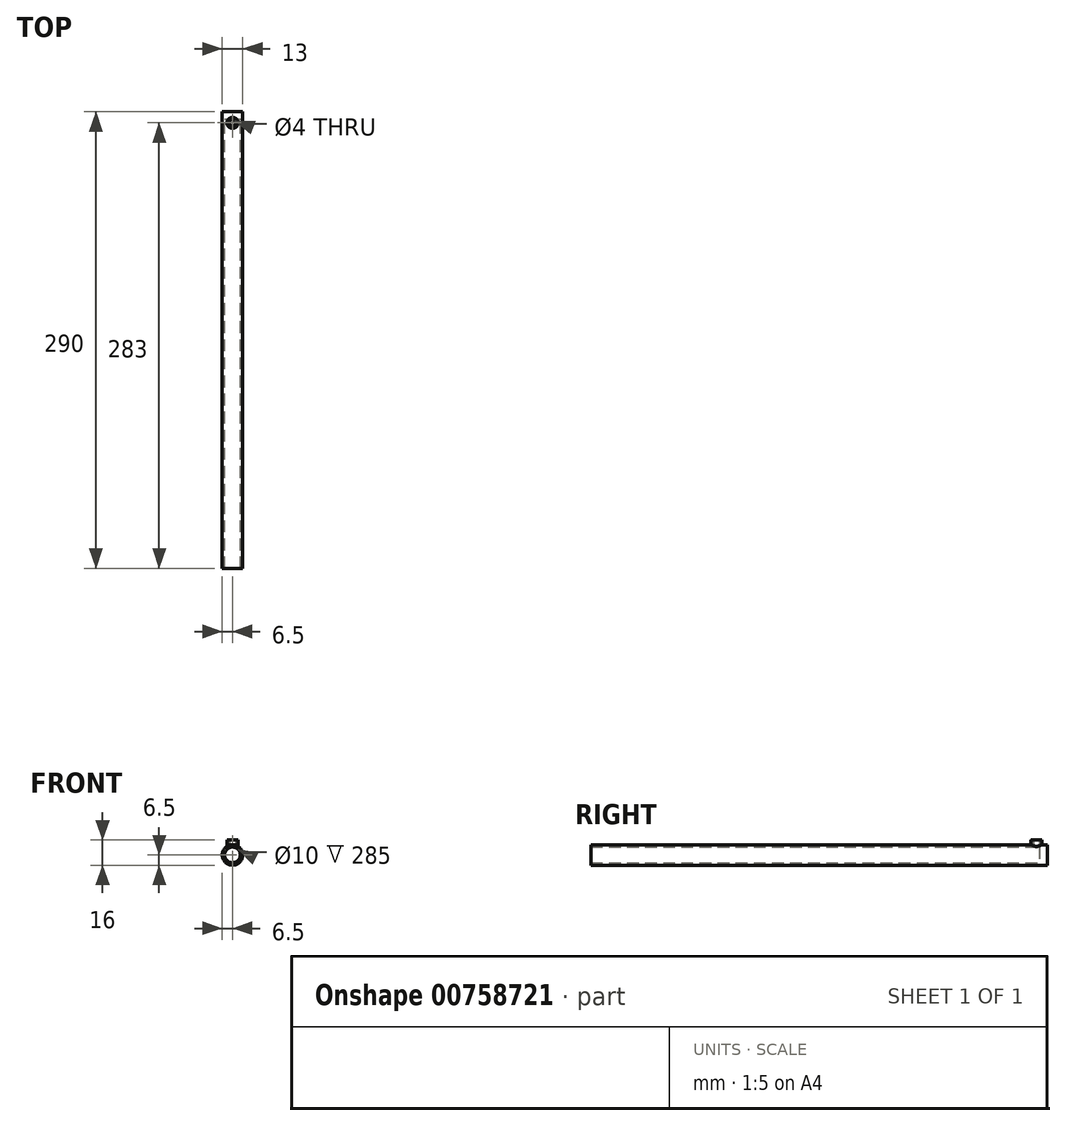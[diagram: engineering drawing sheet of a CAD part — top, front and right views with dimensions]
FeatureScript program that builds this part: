
annotation { "Feature Type Name" : "Feature", "Feature Type Description" : "" }
export const myFeature = defineFeature(function(context is Context, id is Id, definition is map)
    precondition{}
    {
        {
            var Q0;
            Q0=qCreatedBy(makeId("Front.planeOp"),FACE);
            var sketch = newSketch(context, id + "F0", { "sketchPlane" : qUnion([Q0])});
            skCircle(sketch, "E0", {"center": v(0, 0) * mm, "radius": 6.5 * mm});
            skCircle(sketch, "E1", {"center": v(0, 0) * mm, "radius": 5 * mm});
            skSolve(sketch);
        }
        {
            var Q0;
            Q0=makeQuery(id+"F0.imprint","IMPRINT",FACE,{"disambiguationData":[TD([[makeQuery(id+"F0.imprint","IMPRINT",EDGE,{"derivedFrom":sQuery(id+"F0.wireOp",EDGE,"E0")}),1.0]])]});
            extrude(context, id + "F1", {"entities" : qUnion([Q0]), "depth" : 290 * mm, "offsetDistance" : 25 * mm});
        }
        {
            var Q0;
            Q0=makeQuery(id+"F0.imprint","IMPRINT",FACE,{"disambiguationData":[TD([[makeQuery(id+"F0.imprint","IMPRINT",EDGE,{"derivedFrom":sQuery(id+"F0.wireOp",EDGE,"E1")}),1.0]])]});
            extrude(context, id + "F2", {"entities" : qUnion([Q0]), "operationType" : NewBodyOperationType.ADD, "depth" : 5 * mm, "offsetDistance" : 25 * mm});
        }
        {
            var Q0;
            Q0=qCreatedBy(makeId("Top.planeOp"),FACE);
            var sketch = newSketch(context, id + "F3", { "sketchPlane" : qUnion([Q0])});
            skLineSegment(sketch, "E2", {"start": v(0, 0) * mm, "end": v(0, -7) * mm});
            skCircle(sketch, "E3", {"center": v(0, -7) * mm, "radius": 2 * mm});
            skCircle(sketch, "E4", {"center": v(0, -7) * mm, "radius": 3.5 * mm});
            skSolve(sketch);
        }
        {
            var Q0;
            Q0=makeQuery(id+"F3.imprint","IMPRINT",FACE,{"disambiguationData":[TD([[makeQuery(id+"F3.imprint","IMPRINT",EDGE,{"derivedFrom":sQuery(id+"F3.wireOp",EDGE,"E3")}),-1.0]])]});
            extrude(context, id + "F4", {"entities" : qUnion([Q0]), "operationType" : NewBodyOperationType.ADD, "depth" : 9.5 * mm, "offsetDistance" : 25 * mm});
        }
        {
            var Q0;
            Q0=makeQuery(id+"F3.imprint","IMPRINT",FACE,{"disambiguationData":[TD([[makeQuery(id+"F3.imprint","IMPRINT",EDGE,{"derivedFrom":sQuery(id+"F3.wireOp",EDGE,"E3")}),1.0]])]});
            extrude(context, id + "F5", {"entities" : qUnion([Q0]), "operationType" : NewBodyOperationType.REMOVE, "depth" : 25 * mm, "offsetDistance" : 25 * mm});
        }
        {
            var Q0;
            Q0=makeQuery(id+"F2.opExtrude","CAP_FACE",FACE,{"disambiguationData":[OSD([sQuery(id+"F0.wireOp",EDGE,"E1")])],"isStart":false});
            extrude(context, id + "F6", {"entities" : qUnion([Q0]), "operationType" : NewBodyOperationType.REMOVE, "depth" : 25 * mm, "offsetDistance" : 25 * mm});
        }
        {
            var Q0;
            Q0=makeQuery(id+"F0.imprint","IMPRINT",FACE,{"disambiguationData":[TD([[makeQuery(id+"F0.imprint","IMPRINT",EDGE,{"derivedFrom":sQuery(id+"F0.wireOp",EDGE,"E1")}),1.0]])]});
            extrude(context, id + "F7", {"entities" : qUnion([Q0]), "operationType" : NewBodyOperationType.REMOVE, "depth" : 25 * mm, "offsetDistance" : 25 * mm, "hasSecondDirection" : true, "secondDirectionOppositeDirection" : false, "secondDirectionDepth" : 5 * mm});
        }
    });
